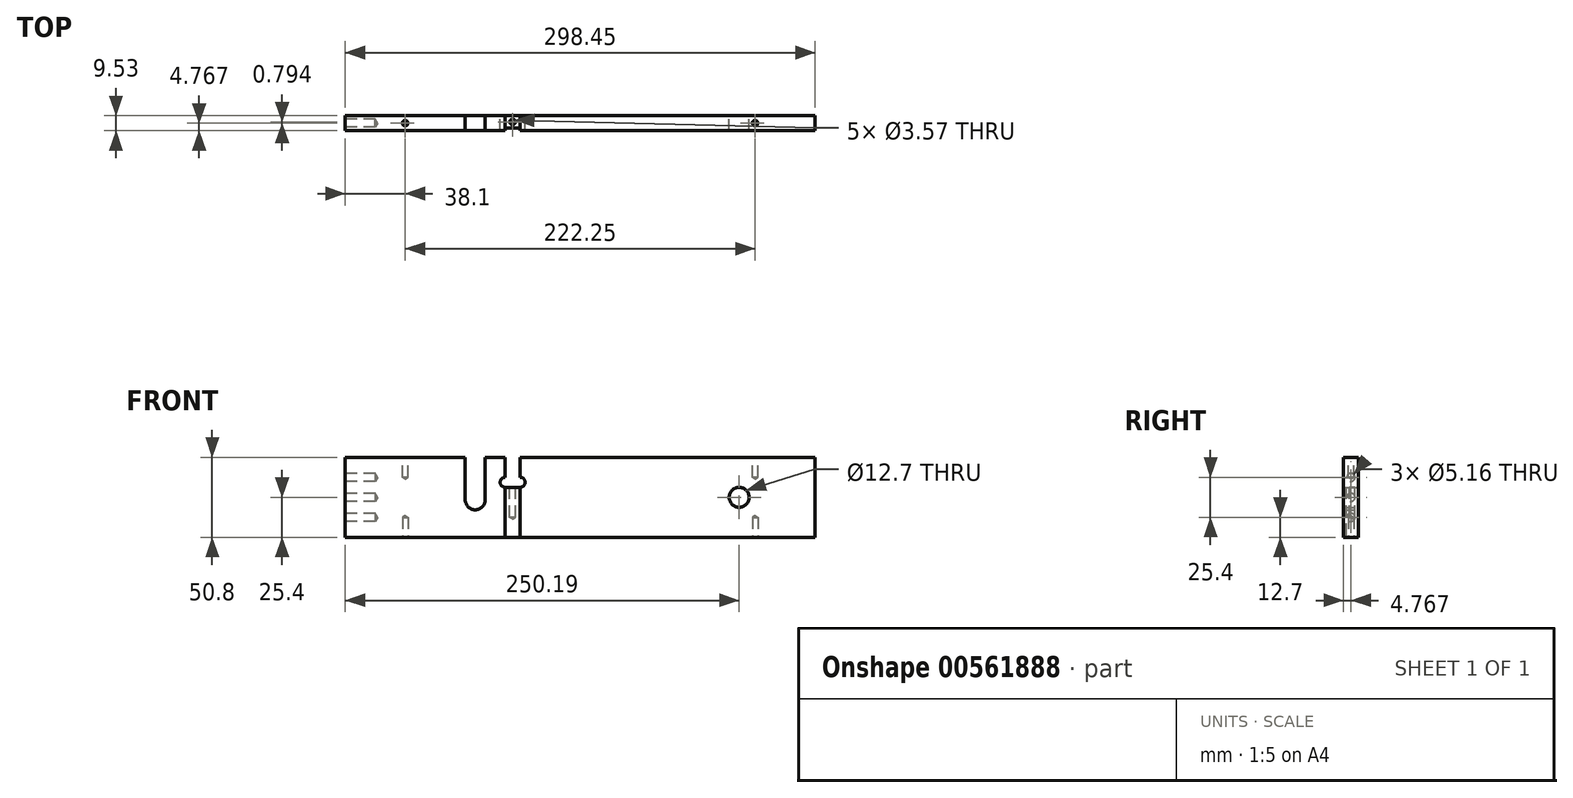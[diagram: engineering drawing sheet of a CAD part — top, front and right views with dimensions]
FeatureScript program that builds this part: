
annotation { "Feature Type Name" : "Feature", "Feature Type Description" : "" }
export const myFeature = defineFeature(function(context is Context, id is Id, definition is map)
    precondition{}
    {
        {
            var Q0;
            Q0=qCreatedBy(makeId("Front.planeOp"),FACE);
            var sketch = newSketch(context, id + "F0", { "sketchPlane" : qUnion([Q0])});
            skLineSegment(sketch, "E0", {"start": v(0, 0) * mm, "end": v(298.45, 0) * mm});
            skLineSegment(sketch, "E1", {"start": v(298.45, 0) * mm, "end": v(298.45, 50.8) * mm});
            skLineSegment(sketch, "E2", {"start": v(0, 50.8) * mm, "end": v(0, 0) * mm});
            skLineSegment(sketch, "E3", {"start": v(0, 50.8) * mm, "end": v(101.6, 50.8) * mm});
            skLineSegment(sketch, "E4", {"start": v(101.6, 50.8) * mm, "end": v(101.6, 31.75) * mm});
            skLineSegment(sketch, "E5", {"start": v(111.14, 50.8) * mm, "end": v(111.14, 31.75) * mm});
            skLineSegment(sketch, "E6", {"start": v(101.6, 31.75) * mm, "end": v(111.14, 31.75) * mm});
            skLineSegment(sketch, "E7", {"start": v(111.14, 50.8) * mm, "end": v(298.45, 50.8) * mm});
            skLineSegment(sketch, "E8", {"start": v(82.55, 50.8) * mm, "end": v(82.55, 0) * mm, "construction": true});
            skArc(sketch, "E9", {"start": v(101.6, 38.1) * mm, "mid": v(98.43, 34.92) * mm, "end": v(101.6, 31.75) * mm});
            skArc(sketch, "E10", {"start": v(111.14, 31.75) * mm, "mid": v(114.31, 34.92) * mm, "end": v(111.14, 38.1) * mm});
            skCircle(sketch, "E11", {"center": v(82.55, 25.4) * mm, "radius": 38.1 * mm, "construction": true});
            skCircle(sketch, "E12", {"center": v(82.55, 23.81) * mm, "radius": 6.35 * mm});
            skLineSegment(sketch, "E13", {"start": v(76.2, 50.8) * mm, "end": v(76.2, 23.81) * mm});
            skLineSegment(sketch, "E14", {"start": v(88.9, 50.8) * mm, "end": v(88.9, 23.81) * mm});
            skCircle(sketch, "E15", {"center": v(250.2, 25.4) * mm, "radius": 38.1 * mm, "construction": true});
            skCircle(sketch, "E16", {"center": v(250.2, 25.4) * mm, "radius": 6.35 * mm});
            skLineSegment(sketch, "E17", {"start": v(250.2, 50.8) * mm, "end": v(250.2, 0) * mm, "construction": true});
            skSolve(sketch);
        }
        {
            var Q0;
            Q0=makeQuery(id+"F0.imprint","IMPRINT",FACE,{"disambiguationData":[TD([[makeQuery(id+"F0.imprint","IMPRINT",EDGE,{"derivedFrom":sQuery(id+"F0.wireOp",EDGE,"E0")}),1.0]])]});
            extrude(context, id + "F1", {"entities" : qUnion([Q0]), "depth" : 9.52 * mm, "offsetDistance" : 25.4 * mm});
        }
        {
            var Q0;
            Q0=makeQuery(id+"F1.opExtrude","CAP_FACE",FACE,{"disambiguationData":[OSD([sQuery(id+"F0.wireOp",EDGE,"E0"),sQuery(id+"F0.wireOp",EDGE,"E1"),sQuery(id+"F0.wireOp",EDGE,"E2"),sQuery(id+"F0.wireOp",EDGE,"E3"),sQuery(id+"F0.wireOp",EDGE,"E4"),sQuery(id+"F0.wireOp",EDGE,"E5"),sQuery(id+"F0.wireOp",EDGE,"E6"),sQuery(id+"F0.wireOp",EDGE,"E7")])],"isStart":false});
            var sketch = newSketch(context, id + "F2", { "sketchPlane" : qUnion([Q0])});
            skLineSegment(sketch, "E18.bottom", {"start": v(111.14, 31.75) * mm, "end": v(101.6, 31.75) * mm});
            skLineSegment(sketch, "E18.top", {"start": v(111.14, 0) * mm, "end": v(101.6, 0) * mm});
            skLineSegment(sketch, "E18.left", {"start": v(111.14, 31.75) * mm, "end": v(111.14, 0) * mm});
            skLineSegment(sketch, "E18.right", {"start": v(101.6, 31.75) * mm, "end": v(101.6, 0) * mm});
            skSolve(sketch);
        }
        {
            var Q0;
            Q0=makeQuery(id+"F2.imprint","IMPRINT",FACE,{"disambiguationData":[TD([[makeQuery(id+"F2.imprint","IMPRINT",EDGE,{"derivedFrom":sQuery(id+"F2.wireOp",EDGE,"E18.bottom")}),-1.0]])]});
            extrude(context, id + "F3", {"entities" : qUnion([Q0]), "operationType" : NewBodyOperationType.REMOVE, "oppositeDirection" : true, "depth" : 1.59 * mm, "offsetDistance" : 25.4 * mm});
        }
        {
            var Q0;
            Q0=makeQuery(id+"F1.opExtrude","SWEPT_FACE",FACE,{"disambiguationData":[OSD([sQuery(id+"F0.wireOp",EDGE,"E2")])]});
            var sketch = newSketch(context, id + "F4", { "sketchPlane" : qUnion([Q0])});
            skLineSegment(sketch, "E19", {"start": v(4.76, 50.8) * mm, "end": v(4.76, 0) * mm, "construction": true});
            skLineSegment(sketch, "E20", {"start": v(0, 25.4) * mm, "end": v(9.53, 25.4) * mm, "construction": true});
            skPoint(sketch, "E21", {"position": v(4.76, 25.4) * mm});
            skPoint(sketch, "E22", {"position": v(4.76, 38.1) * mm});
            skPoint(sketch, "E23", {"position": v(4.76, 12.7) * mm});
            skSolve(sketch);
        }
        {
            var Q0;
            Q0=sQuery(id+"F4.wireOp",VERTEX,"E22");
            var Q1;
            Q1=sQuery(id+"F4.wireOp",VERTEX,"E21");
            var Q2;
            Q2=sQuery(id+"F4.wireOp",VERTEX,"E23");
            var Q3;
            Q3=makeQuery(id+"F1.opExtrude","SWEPT_BODY",BODY,{"disambiguationData":[OSD([sQuery(id+"F0.wireOp",EDGE,"E0"),sQuery(id+"F0.wireOp",EDGE,"E1"),sQuery(id+"F0.wireOp",EDGE,"E2"),sQuery(id+"F0.wireOp",EDGE,"E3"),sQuery(id+"F0.wireOp",EDGE,"E4"),sQuery(id+"F0.wireOp",EDGE,"E5"),sQuery(id+"F0.wireOp",EDGE,"E6"),sQuery(id+"F0.wireOp",EDGE,"E7"),sQuery(id+"F0.wireOp",EDGE,"E9"),sQuery(id+"F0.wireOp",EDGE,"E10"),sQuery(id+"F0.wireOp",EDGE,"E12"),sQuery(id+"F0.wireOp",EDGE,"E13"),sQuery(id+"F0.wireOp",EDGE,"E14"),sQuery(id+"F0.wireOp",EDGE,"E16")])]});
            hole(context, id + "F5", {"style" : HoleStyle.SIMPLE, "endStyle" : HoleEndStyle.BLIND, "holeDiameter" : 5.16 * mm, "majorDiameter" : 6.35 * mm, "holeDepth" : 19.05 * mm, "isTappedThrough" : true, "tappedDepth" : 12.7 * mm, "tapClearance" : 3, "startFromSketch" : true, "locations" : qUnion([Q0, Q1, Q2]), "scope" : qUnion([Q3])});
        }
        {
            var Q0;
            Q0=makeQuery(id+"F1.opExtrude","SWEPT_FACE",FACE,{"disambiguationData":[OSD([sQuery(id+"F0.wireOp",EDGE,"E6")])]});
            var sketch = newSketch(context, id + "F6", { "sketchPlane" : qUnion([Q0])});
            skLineSegment(sketch, "E24.bottom", {"start": v(101.6, 0) * mm, "end": v(111.14, 0) * mm, "construction": true});
            skLineSegment(sketch, "E24.top", {"start": v(101.6, -7.94) * mm, "end": v(111.14, -7.94) * mm, "construction": true});
            skLineSegment(sketch, "E24.left", {"start": v(101.6, 0) * mm, "end": v(101.6, -7.94) * mm, "construction": true});
            skLineSegment(sketch, "E24.right", {"start": v(111.14, 0) * mm, "end": v(111.14, -7.94) * mm, "construction": true});
            skLineSegment(sketch, "E25", {"start": v(101.6, -7.94) * mm, "end": v(111.14, 0) * mm, "construction": true});
            skLineSegment(sketch, "E26", {"start": v(101.6, 0) * mm, "end": v(111.14, -7.94) * mm, "construction": true});
            skPoint(sketch, "E27", {"position": v(106.37, -3.97) * mm});
            skSolve(sketch);
        }
        {
            var Q0;
            Q0=sQuery(id+"F6.wireOp",VERTEX,"E27");
            var Q1;
            Q1=makeQuery(id+"F1.opExtrude","SWEPT_BODY",BODY,{"disambiguationData":[OSD([sQuery(id+"F0.wireOp",EDGE,"E0"),sQuery(id+"F0.wireOp",EDGE,"E1"),sQuery(id+"F0.wireOp",EDGE,"E2"),sQuery(id+"F0.wireOp",EDGE,"E3"),sQuery(id+"F0.wireOp",EDGE,"E4"),sQuery(id+"F0.wireOp",EDGE,"E5"),sQuery(id+"F0.wireOp",EDGE,"E6"),sQuery(id+"F0.wireOp",EDGE,"E7"),sQuery(id+"F0.wireOp",EDGE,"E9"),sQuery(id+"F0.wireOp",EDGE,"E10"),sQuery(id+"F0.wireOp",EDGE,"E12"),sQuery(id+"F0.wireOp",EDGE,"E13"),sQuery(id+"F0.wireOp",EDGE,"E14"),sQuery(id+"F0.wireOp",EDGE,"E16")])]});
            hole(context, id + "F7", {"style" : HoleStyle.SIMPLE, "endStyle" : HoleEndStyle.BLIND, "holeDiameter" : 3.57 * mm, "majorDiameter" : 6.35 * mm, "holeDepth" : 19.05 * mm, "isTappedThrough" : true, "tappedDepth" : 12.7 * mm, "tapClearance" : 3, "startFromSketch" : true, "locations" : qUnion([Q0]), "scope" : qUnion([Q1])});
        }
        {
            var Q0;
            {var subQ0=sQuery(id+"F0.wireOp",EDGE,"E3");Q0=makeQuery(id+"F1.opExtrude","SWEPT_FACE",FACE,{"disambiguationData":[OSD([subQ0]),TDD([makeQuery(id+"F0.imprint","IMPRINT",EDGE,{"disambiguationData":[TD([[makeQuery(id+"F0.imprint","INTERSECT",VERTEX,{"derivedFrom":[sQuery(id+"F0.wireOp",EDGE,"E2"),subQ0]}),-1.0]])],"derivedFrom":subQ0})])]});}
            var sketch = newSketch(context, id + "F8", { "sketchPlane" : qUnion([Q0])});
            skLineSegment(sketch, "E28", {"start": v(38.1, 0) * mm, "end": v(38.1, -9.53) * mm});
            skPoint(sketch, "E29", {"position": v(38.1, -4.76) * mm});
            skLineSegment(sketch, "E30", {"start": v(260.35, 0) * mm, "end": v(260.35, -9.52) * mm});
            skPoint(sketch, "E31", {"position": v(260.35, -4.76) * mm});
            skSolve(sketch);
        }
        {
            var Q0;
            Q0=makeQuery(id+"F1.opExtrude","SWEPT_FACE",FACE,{"disambiguationData":[OSD([sQuery(id+"F0.wireOp",EDGE,"E0")])]});
            var sketch = newSketch(context, id + "F9", { "sketchPlane" : qUnion([Q0])});
            skLineSegment(sketch, "E32", {"start": v(38.1, 9.53) * mm, "end": v(38.1, 0) * mm});
            skLineSegment(sketch, "E33", {"start": v(260.35, 9.53) * mm, "end": v(260.35, 0) * mm});
            skPoint(sketch, "E34", {"position": v(260.35, 4.76) * mm});
            skPoint(sketch, "E35", {"position": v(38.1, 4.76) * mm});
            skSolve(sketch);
        }
        {
            var Q0;
            Q0=sQuery(id+"F8.wireOp",VERTEX,"E29");
            var Q1;
            Q1=sQuery(id+"F8.wireOp",VERTEX,"E31");
            var Q2;
            Q2=sQuery(id+"F9.wireOp",VERTEX,"E34");
            var Q3;
            Q3=sQuery(id+"F9.wireOp",VERTEX,"E35");
            var Q4;
            Q4=makeQuery(id+"F1.opExtrude","SWEPT_BODY",BODY,{"disambiguationData":[OSD([sQuery(id+"F0.wireOp",EDGE,"E0"),sQuery(id+"F0.wireOp",EDGE,"E1"),sQuery(id+"F0.wireOp",EDGE,"E2"),sQuery(id+"F0.wireOp",EDGE,"E3"),sQuery(id+"F0.wireOp",EDGE,"E4"),sQuery(id+"F0.wireOp",EDGE,"E5"),sQuery(id+"F0.wireOp",EDGE,"E6"),sQuery(id+"F0.wireOp",EDGE,"E7"),sQuery(id+"F0.wireOp",EDGE,"E9"),sQuery(id+"F0.wireOp",EDGE,"E10"),sQuery(id+"F0.wireOp",EDGE,"E12"),sQuery(id+"F0.wireOp",EDGE,"E13"),sQuery(id+"F0.wireOp",EDGE,"E14"),sQuery(id+"F0.wireOp",EDGE,"E16")])]});
            hole(context, id + "F10", {"style" : HoleStyle.SIMPLE, "endStyle" : HoleEndStyle.BLIND, "holeDiameter" : 3.57 * mm, "majorDiameter" : 6.35 * mm, "holeDepth" : 12.7 * mm, "isTappedThrough" : true, "tappedDepth" : 12.7 * mm, "tapClearance" : 3, "startFromSketch" : true, "locations" : qUnion([Q0, Q1, Q2, Q3]), "scope" : qUnion([Q4])});
        }
    });
